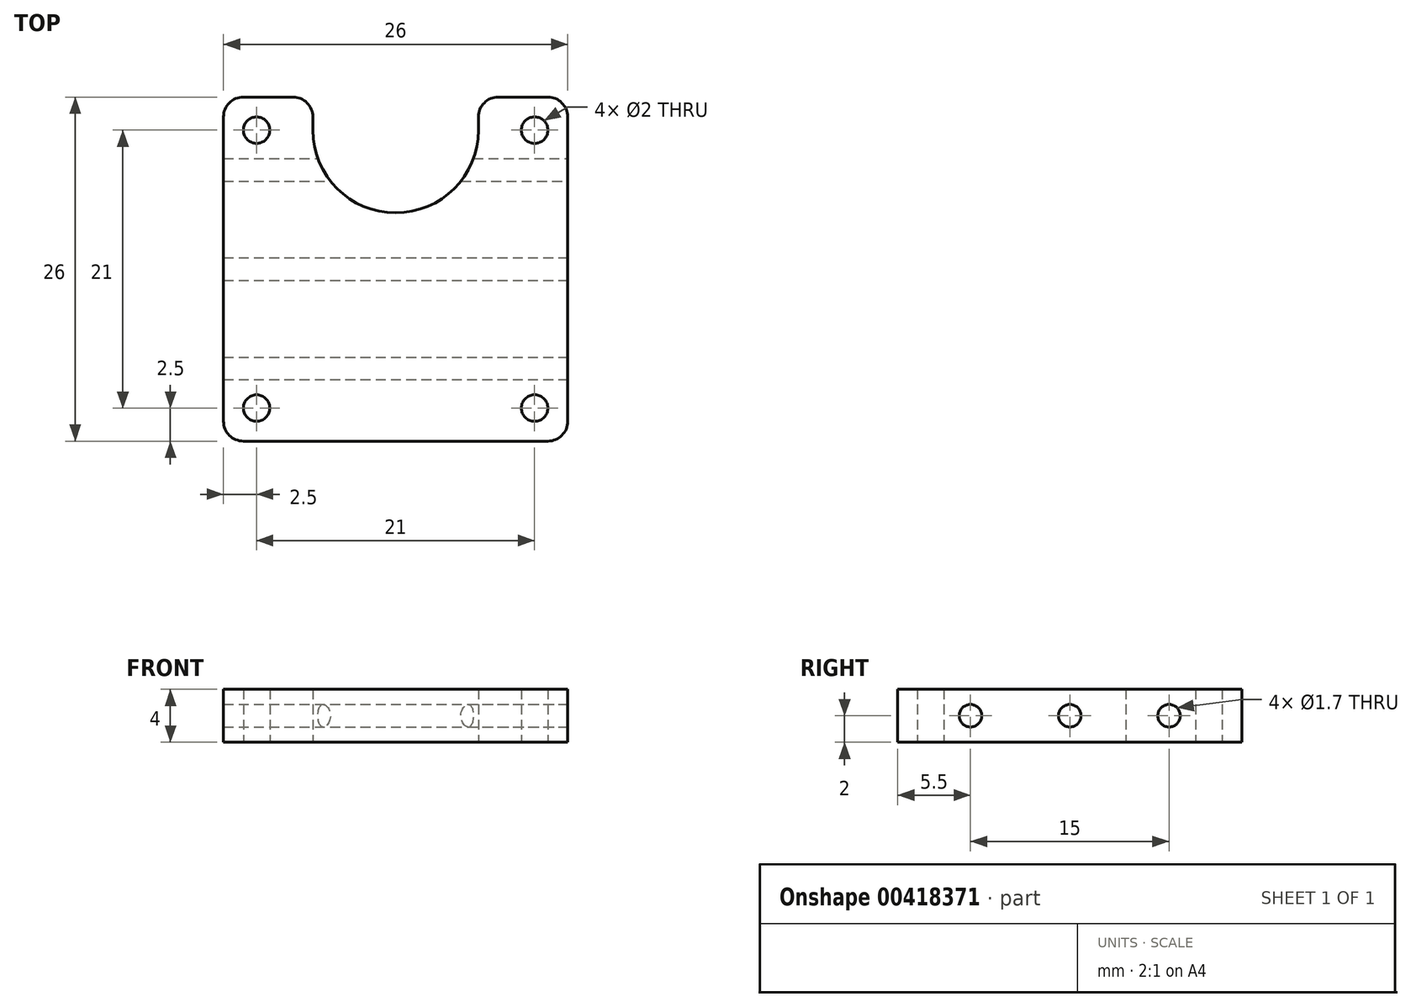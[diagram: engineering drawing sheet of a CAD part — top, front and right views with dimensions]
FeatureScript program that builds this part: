
annotation { "Feature Type Name" : "Feature", "Feature Type Description" : "" }
export const myFeature = defineFeature(function(context is Context, id is Id, definition is map)
    precondition{}
    {
        {
            var Q0;
            Q0=qCreatedBy(makeId("Top.planeOp"),FACE);
            var sketch = newSketch(context, id + "F0", { "sketchPlane" : qUnion([Q0])});
            skArc(sketch, "E0", {"start": v(-6.25, 0) * mm, "mid": v(0, -6.25) * mm, "end": v(6.25, 0) * mm});
            skCircle(sketch, "E1", {"center": v(10.5, 0) * mm, "radius": 1 * mm});
            skCircle(sketch, "E2", {"center": v(10.5, -21) * mm, "radius": 1 * mm});
            skCircle(sketch, "E3.MirrorC", {"center": v(-10.5, 0) * mm, "radius": 1 * mm});
            skCircle(sketch, "E4.MirrorC", {"center": v(-10.5, -21) * mm, "radius": 1 * mm});
            skLineSegment(sketch, "E5.bottom", {"start": v(-13, 2.5) * mm, "end": v(-6.25, 2.5) * mm});
            skLineSegment(sketch, "E5.top", {"start": v(-13, -23.5) * mm, "end": v(13, -23.5) * mm});
            skLineSegment(sketch, "E5.left", {"start": v(-13, 2.5) * mm, "end": v(-13, -23.5) * mm});
            skLineSegment(sketch, "E5.right", {"start": v(13, 2.5) * mm, "end": v(13, -23.5) * mm});
            skPoint(sketch, "E6", {"position": v(0, -23.5) * mm});
            skLineSegment(sketch, "E7", {"start": v(-13, -10.5) * mm, "end": v(13, -10.5) * mm, "construction": true});
            skLineSegment(sketch, "E8", {"start": v(-10.5, 0) * mm, "end": v(-10.5, -21) * mm, "construction": true});
            skPoint(sketch, "E9", {"position": v(-10.5, -10.5) * mm});
            skLineSegment(sketch, "E10", {"start": v(-6.25, 0) * mm, "end": v(-6.25, 2.5) * mm});
            skLineSegment(sketch, "E11.MirrorCS", {"start": v(6.25, 0) * mm, "end": v(6.25, 2.5) * mm});
            skLineSegment(sketch, "E12.trimOffspring", {"start": v(6.25, 2.5) * mm, "end": v(13, 2.5) * mm});
            skLineSegment(sketch, "E13", {"start": v(-13, -3) * mm, "end": v(13, -3) * mm, "construction": true});
            skLineSegment(sketch, "E14.MirrorCS", {"start": v(-13, -18) * mm, "end": v(13, -18) * mm, "construction": true});
            skSolve(sketch);
        }
        {
            var Q0;
            Q0 = qSketchRegion(id + "F0", true);
            extrude(context, id + "F1", {"entities" : qUnion([Q0]), "depth" : 2 * mm, "offsetDistance" : 25 * mm, "hasSecondDirection" : true, "secondDirectionOppositeDirection" : true, "secondDirectionDepth" : 2 * mm});
        }
        {
            var Q0;
            Q0=makeQuery(id+"F1.opExtrude","SWEPT_FACE",FACE,{"disambiguationData":[OSD([sQuery(id+"F0.wireOp",EDGE,"E5.right")])]});
            var sketch = newSketch(context, id + "F2", { "sketchPlane" : qUnion([Q0])});
            skSolve(sketch);
        }
        {
            var Q0;
            {var subQ0=sQuery(id+"F0.wireOp",EDGE,"E5.right");Q0=makeQuery(id+"F2.imprint","IMPRINT",FACE,{"disambiguationData":[TD([[makeQuery(id+"F2.imprint","IMPRINT",EDGE,{"derivedFrom":makeQuery(id+"F1.opExtrude","CAP_EDGE",EDGE,{"disambiguationData":[OSD([subQ0])],"isStart":true})}),-1.0]])]});}
            var sketch = newSketch(context, id + "F3", { "sketchPlane" : qUnion([Q0])});
            skLineSegment(sketch, "E15.0", {"start": v(2.5, 2) * mm, "end": v(-23.5, 2) * mm, "construction": true});
            skLineSegment(sketch, "E16.0", {"start": v(2.5, -2) * mm, "end": v(-23.5, -2) * mm, "construction": true});
            skLineSegment(sketch, "E17", {"start": v(-10.5, 2) * mm, "end": v(-10.5, -2) * mm, "construction": true});
            skCircle(sketch, "E18", {"center": v(-10.5, 0) * mm, "radius": 0.85 * mm});
            skCircle(sketch, "E19", {"center": v(-3, 0) * mm, "radius": 0.85 * mm});
            skCircle(sketch, "E20.MirrorC", {"center": v(-18, 0) * mm, "radius": 0.85 * mm});
            skSolve(sketch);
        }
        {
            var Q0;
            Q0 = qSketchRegion(id + "F3", true);
            extrude(context, id + "F4", {"entities" : qUnion([Q0]), "operationType" : NewBodyOperationType.REMOVE, "endBound" : BoundingType.THROUGH_ALL, "oppositeDirection" : true, "depth" : 25 * mm, "offsetDistance" : 25 * mm});
        }
        {
            var Q0;
            Q0=makeQuery(id+"F1.opExtrude","SWEPT_EDGE",EDGE,{"disambiguationData":[OSD([sQuery(id+"F0.wireOp",EDGE,"E5.bottom"),sQuery(id+"F0.wireOp",EDGE,"E5.left")])]});
            var Q1;
            Q1=makeQuery(id+"F1.opExtrude","SWEPT_EDGE",EDGE,{"disambiguationData":[OSD([sQuery(id+"F0.wireOp",EDGE,"E5.right"),sQuery(id+"F0.wireOp",EDGE,"E12.trimOffspring")])]});
            var Q2;
            Q2=makeQuery(id+"F1.opExtrude","SWEPT_EDGE",EDGE,{"disambiguationData":[OSD([sQuery(id+"F0.wireOp",EDGE,"E11.MirrorCS"),sQuery(id+"F0.wireOp",EDGE,"E12.trimOffspring")])]});
            var Q3;
            Q3=makeQuery(id+"F1.opExtrude","SWEPT_EDGE",EDGE,{"disambiguationData":[OSD([sQuery(id+"F0.wireOp",EDGE,"E5.bottom"),sQuery(id+"F0.wireOp",EDGE,"E10")])]});
            var Q4;
            Q4=makeQuery(id+"F1.opExtrude","SWEPT_EDGE",EDGE,{"disambiguationData":[OSD([sQuery(id+"F0.wireOp",EDGE,"E5.top"),sQuery(id+"F0.wireOp",EDGE,"E5.left")])]});
            var Q5;
            Q5=makeQuery(id+"F1.opExtrude","SWEPT_EDGE",EDGE,{"disambiguationData":[OSD([sQuery(id+"F0.wireOp",EDGE,"E5.top"),sQuery(id+"F0.wireOp",EDGE,"E5.right")])]});
            fillet(context, id + "F5", {"entities" : qUnion([Q0, Q1, Q2, Q3, Q4, Q5]), "radius" : 1.5 * mm, "tangentPropagation" : true, "allowEdgeOverflow" : false});
        }
    });
